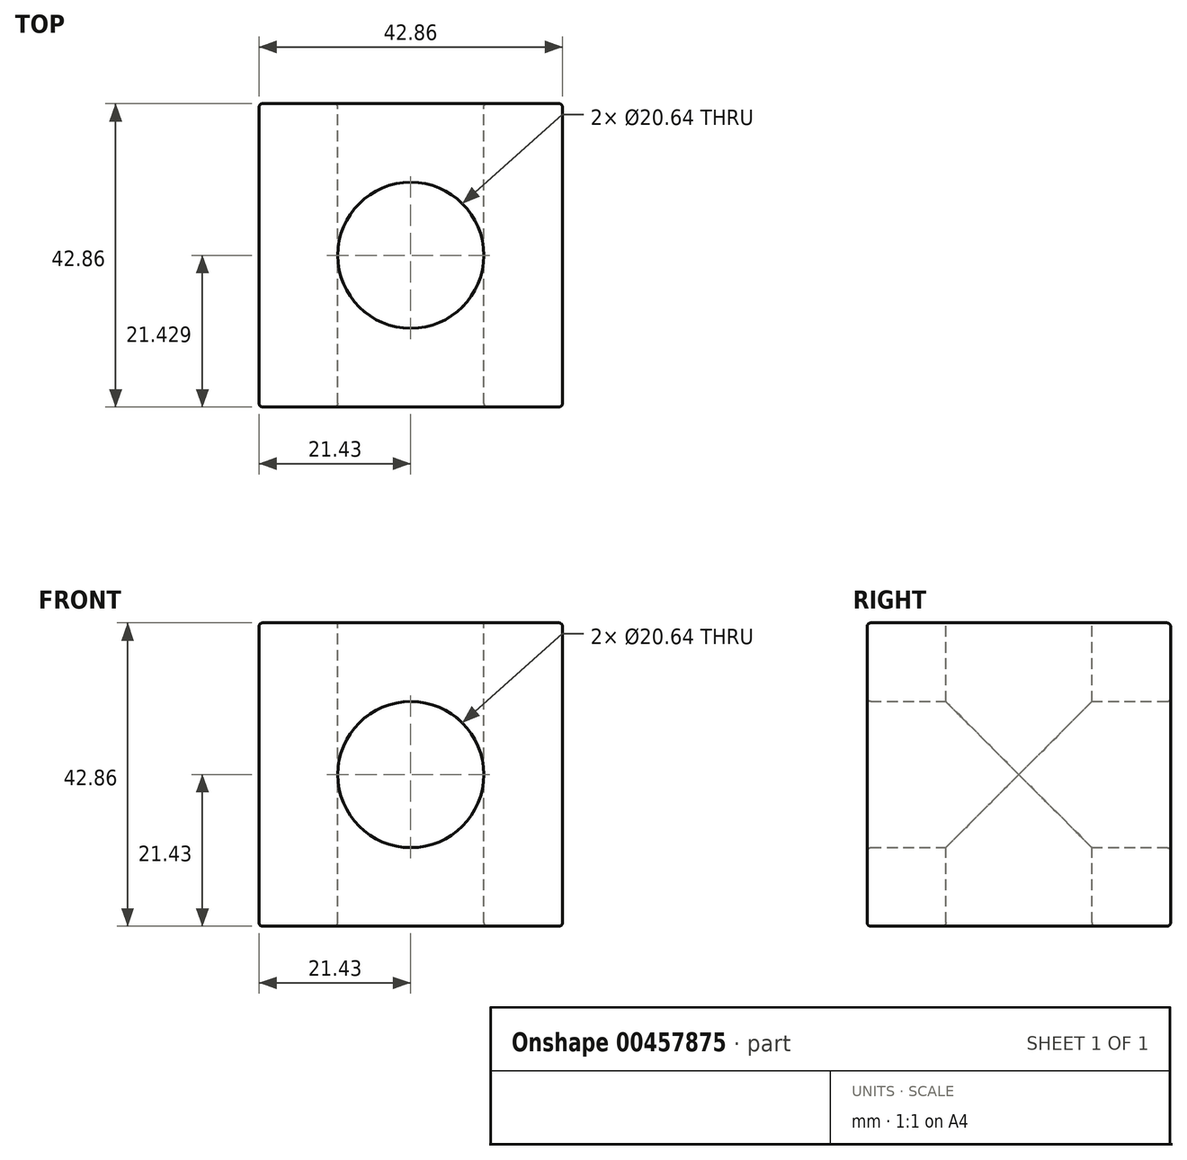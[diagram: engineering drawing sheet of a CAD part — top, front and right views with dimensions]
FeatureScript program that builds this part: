
annotation { "Feature Type Name" : "Feature", "Feature Type Description" : "" }
export const myFeature = defineFeature(function(context is Context, id is Id, definition is map)
    precondition{}
    {
        {
            var Q0;
            Q0=qCreatedBy(makeId("Front.planeOp"),FACE);
            var sketch = newSketch(context, id + "F0", { "sketchPlane" : qUnion([Q0])});
            skLineSegment(sketch, "E0.bottom", {"start": v(21.43, 21.43) * mm, "end": v(-21.43, 21.43) * mm});
            skLineSegment(sketch, "E0.top", {"start": v(21.43, -21.43) * mm, "end": v(-21.43, -21.43) * mm});
            skLineSegment(sketch, "E0.left", {"start": v(21.43, 21.43) * mm, "end": v(21.43, -21.43) * mm});
            skLineSegment(sketch, "E0.right", {"start": v(-21.43, 21.43) * mm, "end": v(-21.43, -21.43) * mm});
            skPoint(sketch, "E0.middle", {"position": v(0, 0) * mm});
            skCircle(sketch, "E1", {"center": v(0, 0) * mm, "radius": 10.32 * mm});
            skSolve(sketch);
        }
        {
            var Q0;
            Q0 = qSketchRegion(id + "F0", true);
            extrude(context, id + "F1", {"entities" : qUnion([Q0]), "depth" : 42.86 * mm});
        }
        {
            var Q0;
            Q0=makeQuery(id+"F1.opExtrude","SWEPT_FACE",FACE,{"disambiguationData":[OSD([sQuery(id+"F0.wireOp",EDGE,"E0.bottom")])]});
            var sketch = newSketch(context, id + "F2", { "sketchPlane" : qUnion([Q0])});
            skCircle(sketch, "E2", {"center": v(0, -21.43) * mm, "radius": 10.32 * mm});
            skSolve(sketch);
        }
        {
            var Q0;
            Q0 = qSketchRegion(id + "F2", true);
            extrude(context, id + "F3", {"entities" : qUnion([Q0]), "operationType" : NewBodyOperationType.REMOVE, "endBound" : BoundingType.THROUGH_ALL, "oppositeDirection" : true, "depth" : 42.93 * mm});
        }
        {
            var Q0;
            Q0=makeQuery(id+"F1.opExtrude","CAP_EDGE",EDGE,{"disambiguationData":[OSD([sQuery(id+"F0.wireOp",EDGE,"E0.bottom")])],"isStart":false});
            fillet(context, id + "F4", {"entities" : qUnion([Q0]), "radius" : 0.5 * mm, "tangentPropagation" : true, "allowEdgeOverflow" : false});
        }
        {
            var Q0;
            Q0=makeQuery(id+"F1.opExtrude","SWEPT_EDGE",EDGE,{"disambiguationData":[OSD([sQuery(id+"F0.wireOp",EDGE,"E0.bottom"),sQuery(id+"F0.wireOp",EDGE,"E0.left")])]});
            var Q1;
            Q1=makeQuery(id+"F1.opExtrude","CAP_EDGE",EDGE,{"disambiguationData":[OSD([sQuery(id+"F0.wireOp",EDGE,"E0.left")])],"isStart":true});
            var Q2;
            Q2=makeQuery(id+"F1.opExtrude","SWEPT_EDGE",EDGE,{"disambiguationData":[OSD([sQuery(id+"F0.wireOp",EDGE,"E0.top"),sQuery(id+"F0.wireOp",EDGE,"E0.left")])]});
            var Q3;
            Q3=makeQuery(id+"F1.opExtrude","CAP_EDGE",EDGE,{"disambiguationData":[OSD([sQuery(id+"F0.wireOp",EDGE,"E0.right")])],"isStart":false});
            var Q4;
            Q4=makeQuery(id+"F1.opExtrude","CAP_EDGE",EDGE,{"disambiguationData":[OSD([sQuery(id+"F0.wireOp",EDGE,"E0.top")])],"isStart":false});
            var Q5;
            Q5=makeQuery(id+"F1.opExtrude","CAP_EDGE",EDGE,{"disambiguationData":[OSD([sQuery(id+"F0.wireOp",EDGE,"E0.top")])],"isStart":true});
            var Q6;
            Q6=makeQuery(id+"F1.opExtrude","SWEPT_EDGE",EDGE,{"disambiguationData":[OSD([sQuery(id+"F0.wireOp",EDGE,"E0.top"),sQuery(id+"F0.wireOp",EDGE,"E0.right")])]});
            var Q7;
            Q7=makeQuery(id+"F1.opExtrude","CAP_EDGE",EDGE,{"disambiguationData":[OSD([sQuery(id+"F0.wireOp",EDGE,"E0.bottom")])],"isStart":true});
            var Q8;
            Q8=makeQuery(id+"F1.opExtrude","CAP_EDGE",EDGE,{"disambiguationData":[OSD([sQuery(id+"F0.wireOp",EDGE,"E0.left")])],"isStart":false});
            var Q9;
            {var subQ0=sQuery(id+"F0.wireOp",EDGE,"E0.bottom");Q9=makeQuery(id+"F4.opFillet","BLEND_EDGE",EDGE,{"blendedFrom":[makeQuery(id+"F1.opExtrude","CAP_EDGE",EDGE,{"disambiguationData":[OSD([subQ0])],"isStart":false}),makeQuery(id+"F1.opExtrude","CAP_FACE",FACE,{"disambiguationData":[OSD([subQ0,sQuery(id+"F0.wireOp",EDGE,"E0.top"),sQuery(id+"F0.wireOp",EDGE,"E0.left"),sQuery(id+"F0.wireOp",EDGE,"E0.right"),sQuery(id+"F0.wireOp",EDGE,"E1")])],"isStart":false})],"blendedInto":[makeQuery(id+"F1.opExtrude","CAP_FACE",FACE,{"disambiguationData":[OSD([subQ0,sQuery(id+"F0.wireOp",EDGE,"E0.top"),sQuery(id+"F0.wireOp",EDGE,"E0.left"),sQuery(id+"F0.wireOp",EDGE,"E0.right"),sQuery(id+"F0.wireOp",EDGE,"E1")])],"isStart":false})]});}
            var Q10;
            Q10=makeQuery(id+"F1.opExtrude","CAP_EDGE",EDGE,{"disambiguationData":[OSD([sQuery(id+"F0.wireOp",EDGE,"E0.right")])],"isStart":true});
            var Q11;
            Q11=makeQuery(id+"F1.opExtrude","SWEPT_EDGE",EDGE,{"disambiguationData":[OSD([sQuery(id+"F0.wireOp",EDGE,"E0.bottom"),sQuery(id+"F0.wireOp",EDGE,"E0.right")])]});
            fillet(context, id + "F5", {"entities" : qUnion([Q0, Q1, Q2, Q3, Q4, Q5, Q6, Q7, Q8, Q9, Q10, Q11]), "radius" : 0.5 * mm, "tangentPropagation" : true, "allowEdgeOverflow" : false});
        }
        {
            var Q0;
            Q0=makeQuery(id+"F1.opExtrude","CAP_EDGE",EDGE,{"disambiguationData":[OSD([sQuery(id+"F0.wireOp",EDGE,"E1")])],"isStart":false});
            var Q1;
            Q1=makeQuery(id+"F3.boolean.opBoolean","INTERSECT",EDGE,{"derivedFrom":[makeQuery(id+"F1.opExtrude","SWEPT_FACE",FACE,{"disambiguationData":[OSD([sQuery(id+"F0.wireOp",EDGE,"E0.top")])]}),makeQuery(id+"F3.opExtrude","SWEPT_FACE",FACE,{"disambiguationData":[OSD([sQuery(id+"F2.wireOp",EDGE,"E2")])]})]});
            var Q2;
            Q2=makeQuery(id+"F3.boolean.opBoolean","COPY",EDGE,{"derivedFrom":makeQuery(id+"F3.opExtrude","CAP_EDGE",EDGE,{"disambiguationData":[OSD([sQuery(id+"F2.wireOp",EDGE,"E2")])],"isStart":true})});
            var Q3;
            Q3=makeQuery(id+"F1.opExtrude","CAP_EDGE",EDGE,{"disambiguationData":[OSD([sQuery(id+"F0.wireOp",EDGE,"E1")])],"isStart":true});
            fillet(context, id + "F6", {"entities" : qUnion([Q0, Q1, Q2, Q3]), "radius" : 0.5 * mm, "tangentPropagation" : true, "allowEdgeOverflow" : false});
        }
    });
